# Revit family: Toilet-Floor_Mount_Hidden_Cord-KOHLER-Veil-K-31193K_1
name_source: partatom
category: Plumbing Fixtures
units: mm (PartAtom-declared; Revit-internal decimal feet)

## family parameters
Cut with Voids When Loaded = No
Host = Face
OmniClass Number = 23.31.19.00
OmniClass Title = Toilets
Part Type = Normal
Room Calculation Point = No
Round Connector Dimension = Use Diameter
Shared = No

## types (1)
- 0-White
    ADA Compliant = No
    Assembly Code = D2010100
    Bowl  Height = 15 3/4"
    CW Connection = Yes
    Cold Water Inlet = Cold Water Inlet
    Date Modified = 04/12/2023
    Default Elevation = 0"
    Description = 2PC Toilet, 2.6/4L, S-trap 305mm
    Finish = Kohler-Vitreous_China-0-White
    Flow Rate = 0 GPM
    Flush Rate- GPF = 2.6 GPF
    Flush Rate- LPF = 4 LPF
    HW Connection = No
    Height = 29 3/8"
    Hot Water Inlet = Hot Water Inlet
    Length = 26 3/4"
    Manufacturer = Kohler Co.
    Master Format 2014 = 22 42 13.13
    Master Format 2014 Name = Residential Water Closets
    Material = Vitreous China
    Model = K-31193K-HC-0
    Pressure = 0.00 psi
    Product Documentation Link = https://resources.kohler.com
    Product Name = Veil
    Product Page URL = https://www.kohlerasiapacific.com
    Rough-In = 12"
    Seat Included = Yes
    Type = 1
    URL = https://www.kohlerasiapacific.com
    Vent Connection = No
    Waste Connection = Yes
    Waste Water Outlet = Waste Water Outlet
    WaterSense Certified = No
    Width = 15"

## geometry (parser evidence)
native form markers: Sweep x5
no freeform markers — native parametric forms only
